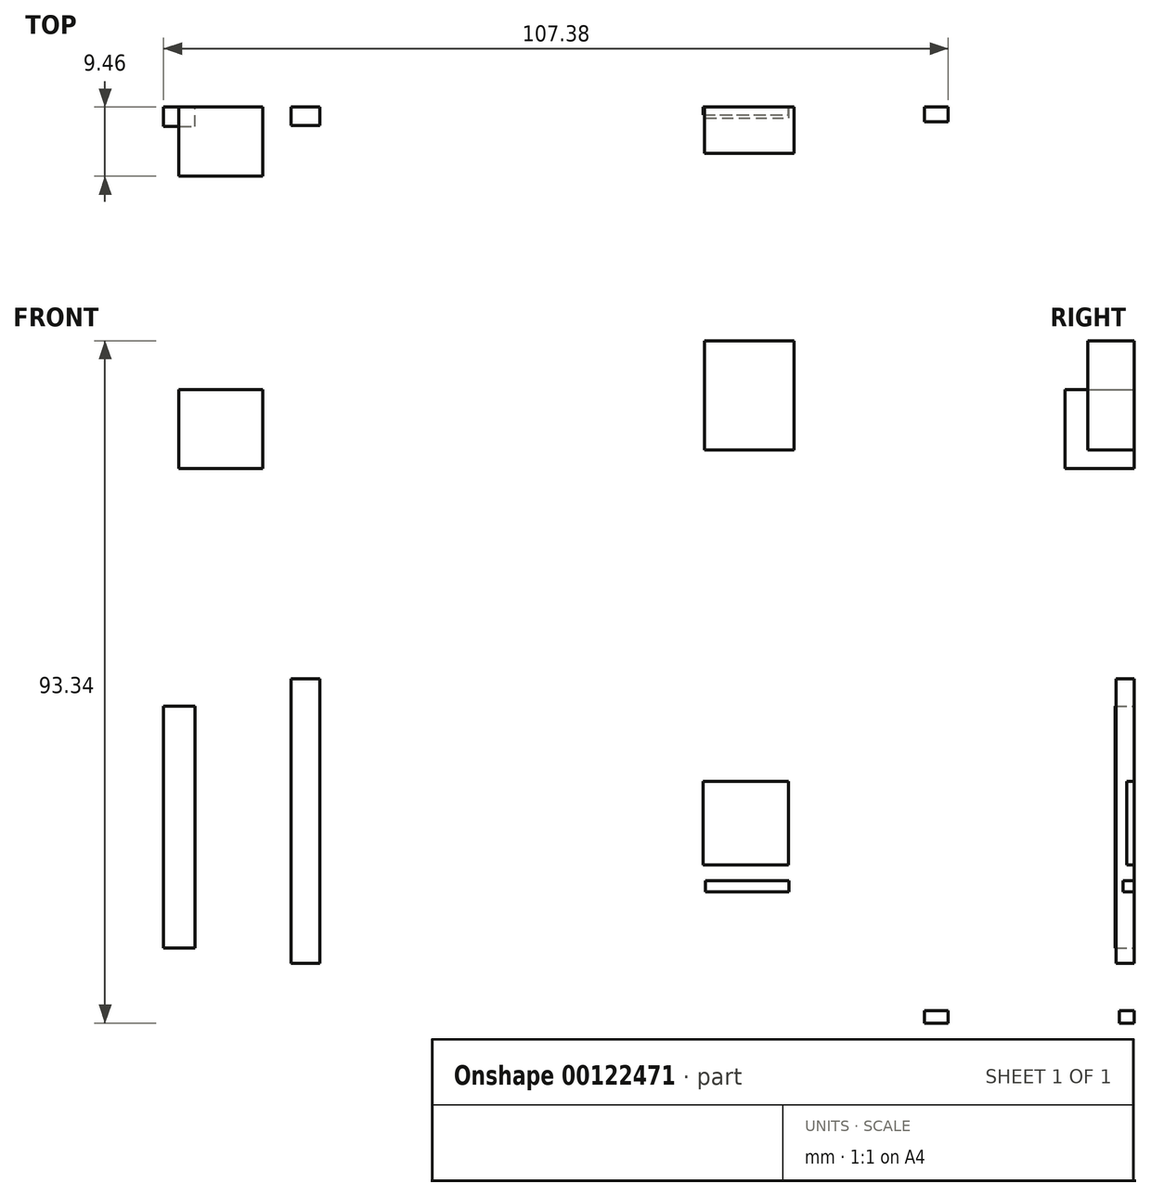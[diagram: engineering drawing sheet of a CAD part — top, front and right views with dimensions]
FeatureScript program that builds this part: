
annotation { "Feature Type Name" : "Feature", "Feature Type Description" : "" }
export const myFeature = defineFeature(function(context is Context, id is Id, definition is map)
    precondition{}
    {
        {
            var Q0;
            Q0=qCreatedBy(makeId("Front.planeOp"),FACE);
            var sketch = newSketch(context, id + "F0", { "sketchPlane" : qUnion([Q0])});
            skLineSegment(sketch, "E0.bottom", {"start": v(-54.32, -16.62) * mm, "end": v(-49.99, -16.62) * mm});
            skLineSegment(sketch, "E0.top", {"start": v(-54.32, -49.7) * mm, "end": v(-49.99, -49.7) * mm});
            skLineSegment(sketch, "E0.left", {"start": v(-54.32, -16.62) * mm, "end": v(-54.32, -49.7) * mm});
            skLineSegment(sketch, "E0.right", {"start": v(-49.99, -16.62) * mm, "end": v(-49.99, -49.7) * mm});
            skPoint(sketch, "E1.firstSnap0", {"position": v(-52.15, -16.62) * mm});
            skLineSegment(sketch, "E1.bottom", {"start": v(-52.15, 27.09) * mm, "end": v(-37.42, 27.09) * mm});
            skLineSegment(sketch, "E1.top", {"start": v(-52.15, 15.08) * mm, "end": v(-37.42, 15.08) * mm});
            skLineSegment(sketch, "E1.left", {"start": v(-52.15, 27.09) * mm, "end": v(-52.15, 15.08) * mm});
            skLineSegment(sketch, "E1.right", {"start": v(-37.42, 27.09) * mm, "end": v(-37.42, 15.08) * mm});
            skSolve(sketch);
        }
        {
            var Q0;
            Q0=makeQuery(id+"F0.imprint","IMPRINT",FACE,{"disambiguationData":[TD([[makeQuery(id+"F0.imprint","IMPRINT",EDGE,{"derivedFrom":sQuery(id+"F0.wireOp",EDGE,"E0.bottom")}),-1.0]])]});
            extrude(context, id + "F1", {"entities" : qUnion([Q0]), "depth" : 2.62 * mm});
        }
        {
            var Q0;
            Q0=qCreatedBy(makeId("Front.planeOp"),FACE);
            var sketch = newSketch(context, id + "F2", { "sketchPlane" : qUnion([Q0])});
            skLineSegment(sketch, "E2.bottom", {"start": v(-36.86, -12.85) * mm, "end": v(-32.95, -12.85) * mm});
            skLineSegment(sketch, "E2.top", {"start": v(-36.86, -51.8) * mm, "end": v(-32.95, -51.8) * mm});
            skLineSegment(sketch, "E2.left", {"start": v(-36.86, -12.85) * mm, "end": v(-36.86, -51.8) * mm});
            skLineSegment(sketch, "E2.right", {"start": v(-32.95, -12.85) * mm, "end": v(-32.95, -51.8) * mm});
            skSolve(sketch);
        }
        {
            var Q0;
            Q0=makeQuery(id+"F2.imprint","IMPRINT",FACE,{"disambiguationData":[TD([[makeQuery(id+"F2.imprint","IMPRINT",EDGE,{"derivedFrom":sQuery(id+"F2.wireOp",EDGE,"E2.bottom")}),-1.0]])]});
            extrude(context, id + "F3", {"entities" : qUnion([Q0]), "depth" : 2.52 * mm});
        }
        {
            var Q0;
            Q0=qCreatedBy(makeId("Front.planeOp"),FACE);
            var sketch = newSketch(context, id + "F4", { "sketchPlane" : qUnion([Q0])});
            skLineSegment(sketch, "E3.bottom", {"start": v(19.69, 33.37) * mm, "end": v(31.98, 33.37) * mm});
            skLineSegment(sketch, "E3.top", {"start": v(19.69, 18.43) * mm, "end": v(31.98, 18.43) * mm});
            skLineSegment(sketch, "E3.left", {"start": v(19.69, 33.37) * mm, "end": v(19.69, 18.43) * mm});
            skLineSegment(sketch, "E3.right", {"start": v(31.98, 33.37) * mm, "end": v(31.98, 18.43) * mm});
            skSolve(sketch);
        }
        {
            var Q0;
            Q0=makeQuery(id+"F4.imprint","IMPRINT",FACE,{"disambiguationData":[TD([[makeQuery(id+"F4.imprint","IMPRINT",EDGE,{"derivedFrom":sQuery(id+"F4.wireOp",EDGE,"E3.bottom")}),-1.0]])]});
            extrude(context, id + "F5", {"entities" : qUnion([Q0]), "depth" : 6.35 * mm});
        }
        {
            var Q0;
            Q0=qCreatedBy(makeId("Front.planeOp"),FACE);
            var sketch = newSketch(context, id + "F6", { "sketchPlane" : qUnion([Q0])});
            skLineSegment(sketch, "E4.bottom", {"start": v(-52.22, 15.92) * mm, "end": v(-40.77, 15.92) * mm});
            skLineSegment(sketch, "E4.top", {"start": v(-52.22, 26.67) * mm, "end": v(-40.77, 26.67) * mm});
            skLineSegment(sketch, "E4.left", {"start": v(-52.22, 15.92) * mm, "end": v(-52.22, 26.67) * mm});
            skLineSegment(sketch, "E4.right", {"start": v(-40.77, 15.92) * mm, "end": v(-40.77, 26.67) * mm});
            skSolve(sketch);
        }
        {
            var Q0;
            Q0=makeQuery(id+"F6.imprint","IMPRINT",FACE,{"disambiguationData":[TD([[makeQuery(id+"F6.imprint","IMPRINT",EDGE,{"derivedFrom":sQuery(id+"F6.wireOp",EDGE,"E4.bottom")}),1.0]])]});
            extrude(context, id + "F7", {"entities" : qUnion([Q0]), "depth" : 9.46 * mm});
        }
        {
            var Q0;
            Q0=qCreatedBy(makeId("Front.planeOp"),FACE);
            var sketch = newSketch(context, id + "F8", { "sketchPlane" : qUnion([Q0])});
            skLineSegment(sketch, "E5.bottom", {"start": v(-37.86, 23.68) * mm, "end": v(-25.42, 23.68) * mm});
            skLineSegment(sketch, "E5.top", {"start": v(-37.86, -29.46) * mm, "end": v(-25.42, -29.46) * mm});
            skLineSegment(sketch, "E5.left", {"start": v(-37.86, 23.68) * mm, "end": v(-37.86, -29.46) * mm});
            skLineSegment(sketch, "E5.right", {"start": v(-25.42, 23.68) * mm, "end": v(-25.42, -29.46) * mm});
            skLineSegment(sketch, "E6.bottom", {"start": v(-25.42, -29.46) * mm, "end": v(-25.42, -29.46) * mm});
            skLineSegment(sketch, "E6.top", {"start": v(-25.42, -2.9) * mm, "end": v(-25.42, -2.9) * mm});
            skLineSegment(sketch, "E6.left", {"start": v(-25.42, -29.46) * mm, "end": v(-25.42, -2.9) * mm});
            skLineSegment(sketch, "E6.right", {"start": v(-25.42, -29.46) * mm, "end": v(-25.42, -2.9) * mm});
            skLineSegment(sketch, "E7.bottom", {"start": v(19.5, -26.89) * mm, "end": v(31.21, -26.89) * mm});
            skLineSegment(sketch, "E7.top", {"start": v(19.5, -38.36) * mm, "end": v(31.21, -38.36) * mm});
            skLineSegment(sketch, "E7.left", {"start": v(19.5, -26.89) * mm, "end": v(19.5, -38.36) * mm});
            skLineSegment(sketch, "E7.right", {"start": v(31.21, -26.89) * mm, "end": v(31.21, -38.36) * mm});
            skSolve(sketch);
        }
        {
            var Q0;
            Q0=makeQuery(id+"F8.imprint","IMPRINT",FACE,{"disambiguationData":[TD([[makeQuery(id+"F8.imprint","IMPRINT",EDGE,{"derivedFrom":sQuery(id+"F8.wireOp",EDGE,"E7.bottom")}),-1.0]])]});
            extrude(context, id + "F9", {"entities" : qUnion([Q0]), "depth" : 1.03 * mm});
        }
        {
            var Q0;
            Q0=qCreatedBy(makeId("Top.planeOp"),FACE);
            var sketch = newSketch(context, id + "F10", { "sketchPlane" : qUnion([Q0])});
            skLineSegment(sketch, "E8.bottom", {"start": v(19.69, -1.26) * mm, "end": v(31, -1.26) * mm});
            skLineSegment(sketch, "E8.top", {"start": v(19.69, -2.37) * mm, "end": v(31, -2.37) * mm});
            skLineSegment(sketch, "E8.left", {"start": v(19.69, -1.26) * mm, "end": v(19.69, -2.37) * mm});
            skLineSegment(sketch, "E8.right", {"start": v(31, -1.26) * mm, "end": v(31, -2.37) * mm});
            skSolve(sketch);
        }
        {
            var Q0;
            Q0=sQuery(id+"F10.wireOp",EDGE,"E8.bottom");
            var Q1;
            Q1=sQuery(id+"F10.wireOp",EDGE,"E8.top");
            extrude(context, id + "F11", {"bodyType" : ToolBodyType.SURFACE, "surfaceEntities" : qUnion([Q0, Q1]), "depth" : 1.13 * mm});
        }
        {
            var Q0;
            Q0=qCreatedBy(makeId("Front.planeOp"),FACE);
            var sketch = newSketch(context, id + "F12", { "sketchPlane" : qUnion([Q0])});
            skLineSegment(sketch, "E9.bottom", {"start": v(19.83, -40.5) * mm, "end": v(31.28, -40.5) * mm});
            skLineSegment(sketch, "E9.top", {"start": v(19.83, -42.03) * mm, "end": v(31.28, -42.03) * mm});
            skLineSegment(sketch, "E9.left", {"start": v(19.83, -40.5) * mm, "end": v(19.83, -42.03) * mm});
            skLineSegment(sketch, "E9.right", {"start": v(31.28, -40.5) * mm, "end": v(31.28, -42.03) * mm});
            skSolve(sketch);
        }
        {
            var Q0;
            Q0 = qSketchRegion(id + "F12", true);
            extrude(context, id + "F13", {"entities" : qUnion([Q0]), "depth" : 1.51 * mm});
        }
        {
            var Q0;
            Q0=qCreatedBy(makeId("Front.planeOp"),FACE);
            var sketch = newSketch(context, id + "F14", { "sketchPlane" : qUnion([Q0])});
            skLineSegment(sketch, "E10.bottom", {"start": v(49.8, -58.28) * mm, "end": v(53.06, -58.28) * mm});
            skLineSegment(sketch, "E10.top", {"start": v(49.8, -59.97) * mm, "end": v(53.06, -59.97) * mm});
            skLineSegment(sketch, "E10.left", {"start": v(49.8, -58.28) * mm, "end": v(49.8, -59.97) * mm});
            skLineSegment(sketch, "E10.right", {"start": v(53.06, -58.28) * mm, "end": v(53.06, -59.97) * mm});
            skSolve(sketch);
        }
        {
            var Q0;
            Q0 = qSketchRegion(id + "F14", true);
            extrude(context, id + "F15", {"entities" : qUnion([Q0]), "depth" : 2.04 * mm});
        }
    });
